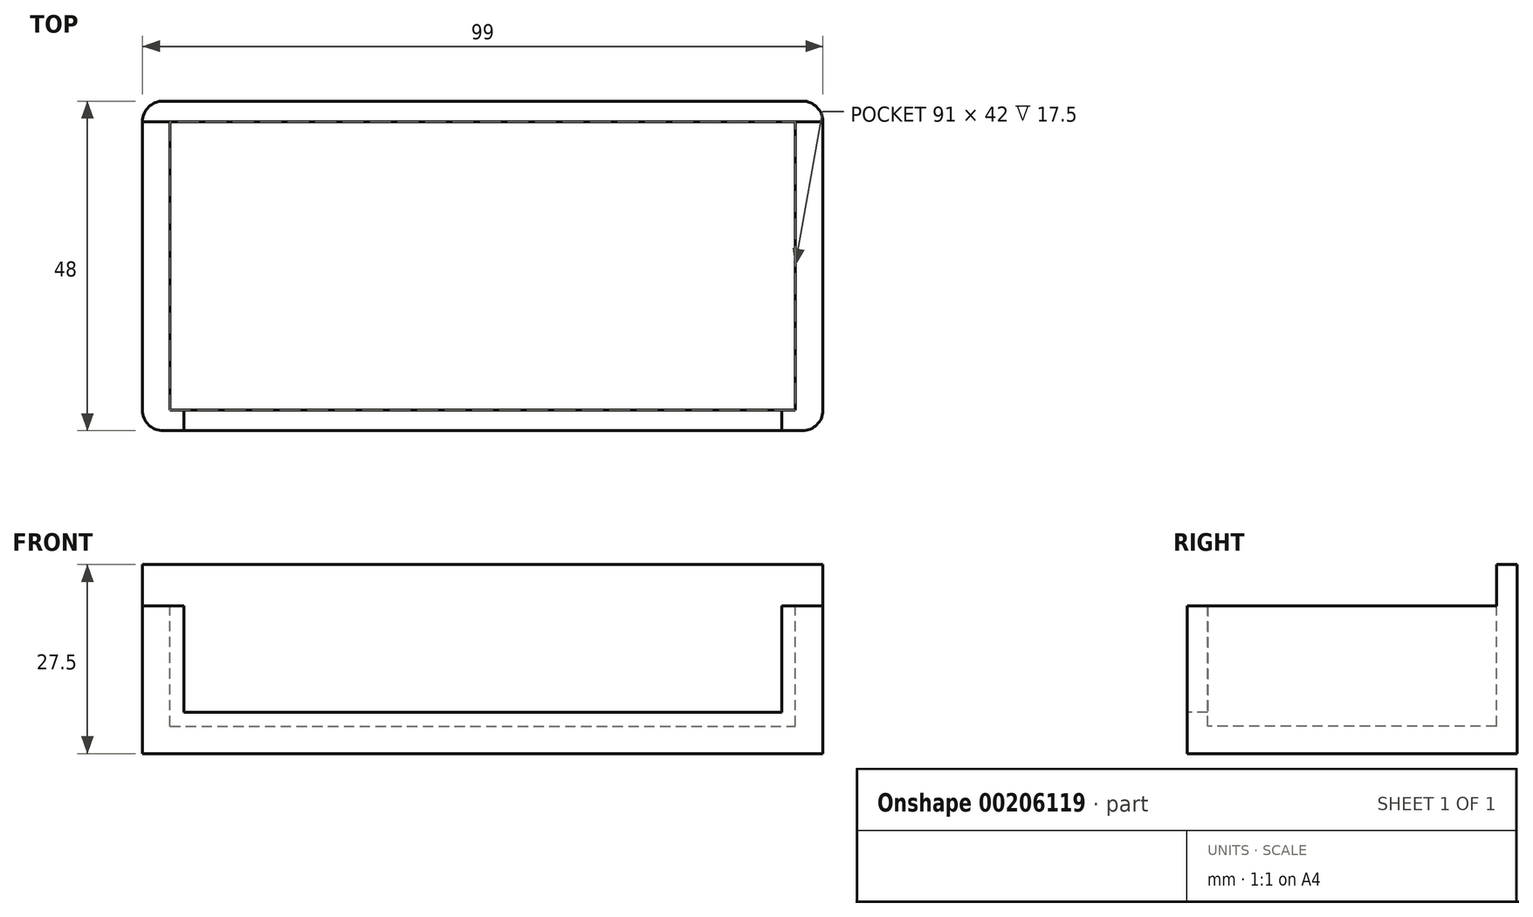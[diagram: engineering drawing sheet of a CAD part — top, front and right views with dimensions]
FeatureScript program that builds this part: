
annotation { "Feature Type Name" : "Feature", "Feature Type Description" : "" }
export const myFeature = defineFeature(function(context is Context, id is Id, definition is map)
    precondition{}
    {
        {
            var Q0;
            Q0=qCreatedBy(makeId("Front.planeOp"),FACE);
            var sketch = newSketch(context, id + "F0", { "sketchPlane" : qUnion([Q0])});
            skLineSegment(sketch, "E0.bottom", {"start": v(-49.5, 6) * mm, "end": v(49.5, 6) * mm});
            skLineSegment(sketch, "E0.top", {"start": v(-49.5, 0) * mm, "end": v(49.5, 0) * mm});
            skLineSegment(sketch, "E0.left", {"start": v(49.5, 6) * mm, "end": v(49.5, 0) * mm});
            skLineSegment(sketch, "E0.right", {"start": v(-49.5, 6) * mm, "end": v(-49.5, 0) * mm});
            skSolve(sketch);
        }
        {
            var Q0;
            Q0=makeQuery(id+"F0.imprint","IMPRINT",FACE,{"disambiguationData":[TD([[makeQuery(id+"F0.imprint","IMPRINT",EDGE,{"derivedFrom":sQuery(id+"F0.wireOp",EDGE,"E0.bottom")}),-1.0]])]});
            extrude(context, id + "F1", {"entities" : qUnion([Q0]), "depth" : 48 * mm});
        }
        {
            var Q0;
            Q0=makeQuery(id+"F1.opExtrude","SWEPT_FACE",FACE,{"disambiguationData":[OSD([sQuery(id+"F0.wireOp",EDGE,"E0.bottom")])]});
            var sketch = newSketch(context, id + "F2", { "sketchPlane" : qUnion([Q0])});
            skLineSegment(sketch, "E1.bottom", {"start": v(49.5, 0) * mm, "end": v(43.5, 0) * mm});
            skLineSegment(sketch, "E1.top", {"start": v(49.5, -48) * mm, "end": v(43.5, -48) * mm});
            skLineSegment(sketch, "E1.left", {"start": v(49.5, 0) * mm, "end": v(49.5, -48) * mm});
            skLineSegment(sketch, "E1.right", {"start": v(43.5, -3) * mm, "end": v(43.5, -48) * mm});
            skLineSegment(sketch, "E2.bottom", {"start": v(49.5, 0) * mm, "end": v(-49.5, 0) * mm});
            skLineSegment(sketch, "E2.top", {"start": v(43.5, -3) * mm, "end": v(-43.5, -3) * mm});
            skLineSegment(sketch, "E2.left", {"start": v(49.5, 0) * mm, "end": v(49.5, -3) * mm});
            skLineSegment(sketch, "E2.right", {"start": v(-49.5, 0) * mm, "end": v(-49.5, -3) * mm});
            skLineSegment(sketch, "E3.bottom", {"start": v(-49.5, 0) * mm, "end": v(-43.5, 0) * mm});
            skLineSegment(sketch, "E3.top", {"start": v(-49.5, -48) * mm, "end": v(-43.5, -48) * mm});
            skLineSegment(sketch, "E3.left", {"start": v(-49.5, 0) * mm, "end": v(-49.5, -48) * mm});
            skLineSegment(sketch, "E3.right", {"start": v(-43.5, -3) * mm, "end": v(-43.5, -48) * mm});
            skSolve(sketch);
        }
        {
            var Q0;
            Q0=makeQuery(id+"F2.imprint","IMPRINT",FACE,{"disambiguationData":[TD([[makeQuery(id+"F2.imprint","IMPRINT",EDGE,{"derivedFrom":sQuery(id+"F2.wireOp",EDGE,"E1.top")}),1.0]])]});
            extrude(context, id + "F3", {"entities" : qUnion([Q0]), "operationType" : NewBodyOperationType.ADD, "depth" : 15.5 * mm});
        }
        {
            var Q0;
            Q0=makeQuery(id+"F3.opExtrude","CAP_FACE",FACE,{"disambiguationData":[OSD([sQuery(id+"F2.wireOp",EDGE,"E1.top"),sQuery(id+"F2.wireOp",EDGE,"E1.left"),sQuery(id+"F2.wireOp",EDGE,"E1.right"),sQuery(id+"F2.wireOp",EDGE,"E2.bottom"),sQuery(id+"F2.wireOp",EDGE,"E2.top"),sQuery(id+"F2.wireOp",EDGE,"E2.left"),sQuery(id+"F2.wireOp",EDGE,"E3.bottom"),sQuery(id+"F2.wireOp",EDGE,"E3.top"),sQuery(id+"F2.wireOp",EDGE,"E3.left"),sQuery(id+"F2.wireOp",EDGE,"E3.right")])],"isStart":false});
            var sketch = newSketch(context, id + "F4", { "sketchPlane" : qUnion([Q0])});
            skLineSegment(sketch, "E4.0", {"start": v(-45.5, -3) * mm, "end": v(-45.5, -45) * mm});
            skLineSegment(sketch, "E5.0", {"start": v(45.5, -3) * mm, "end": v(45.5, -45) * mm});
            skLineSegment(sketch, "E6.0", {"start": v(-45.5, -45) * mm, "end": v(45.5, -45) * mm});
            skLineSegment(sketch, "E7.bottom", {"start": v(-49.5, 0) * mm, "end": v(49.5, 0) * mm});
            skLineSegment(sketch, "E7.top", {"start": v(-49.5, -3) * mm, "end": v(49.5, -3) * mm});
            skLineSegment(sketch, "E7.left", {"start": v(-49.5, 0) * mm, "end": v(-49.5, -3) * mm});
            skLineSegment(sketch, "E7.right", {"start": v(49.5, 0) * mm, "end": v(49.5, -3) * mm});
            skSolve(sketch);
        }
        {
            var Q0;
            {var subQ0=sQuery(id+"F4.wireOp",EDGE,"E4.0");Q0=makeQuery(id+"F4.imprint","IMPRINT",FACE,{"disambiguationData":[TD([[makeQuery(id+"F4.imprint","IMPRINT",EDGE,{"derivedFrom":subQ0}),1.0]])]});}
            var Q1;
            {var subQ0=sQuery(id+"F4.wireOp",EDGE,"E6.0");var subQ1=makeQuery(id+"F3.opExtrude","CAP_EDGE",EDGE,{"disambiguationData":[OSD([sQuery(id+"F2.wireOp",EDGE,"E3.right")])],"isStart":false});var subQ2=makeQuery(id+"F4.imprint","INTERSECT",VERTEX,{"derivedFrom":[subQ1,subQ0]});Q1=makeQuery(id+"F4.imprint","IMPRINT",FACE,{"disambiguationData":[TD([[makeQuery(id+"F4.imprint","IMPRINT",EDGE,{"disambiguationData":[TD([[subQ2,-1.0]])],"derivedFrom":subQ0}),1.0]])]});}
            var Q2;
            {var subQ0=sQuery(id+"F4.wireOp",EDGE,"E5.0");Q2=makeQuery(id+"F4.imprint","IMPRINT",FACE,{"disambiguationData":[TD([[makeQuery(id+"F4.imprint","IMPRINT",EDGE,{"derivedFrom":subQ0}),-1.0]])]});}
            extrude(context, id + "F5", {"entities" : qUnion([Q0, Q1, Q2]), "operationType" : NewBodyOperationType.REMOVE, "oppositeDirection" : true, "depth" : 17.5 * mm});
        }
        {
            var Q0;
            Q0=makeQuery(id+"F4.imprint","IMPRINT",FACE,{"disambiguationData":[TD([[makeQuery(id+"F4.imprint","IMPRINT",EDGE,{"derivedFrom":sQuery(id+"F4.wireOp",EDGE,"E7.bottom")}),-1.0]])]});
            extrude(context, id + "F6", {"entities" : qUnion([Q0]), "operationType" : NewBodyOperationType.ADD, "depth" : 6 * mm});
        }
        {
            var Q0;
            Q0=makeQuery(id+"F3.boolean.opBoolean","MERGE",EDGE,{"derivedFrom":[makeQuery(id+"F1.opExtrude","CAP_EDGE",EDGE,{"disambiguationData":[OSD([sQuery(id+"F0.wireOp",EDGE,"E0.right")])],"isStart":false}),makeQuery(id+"F3.opExtrude","SWEPT_EDGE",EDGE,{"disambiguationData":[OSD([sQuery(id+"F2.wireOp",EDGE,"E3.top"),sQuery(id+"F2.wireOp",EDGE,"E3.left")])]})]});
            var Q1;
            Q1=makeQuery(id+"F3.boolean.opBoolean","MERGE",EDGE,{"derivedFrom":[makeQuery(id+"F1.opExtrude","CAP_EDGE",EDGE,{"disambiguationData":[OSD([sQuery(id+"F0.wireOp",EDGE,"E0.left")])],"isStart":false}),makeQuery(id+"F3.opExtrude","SWEPT_EDGE",EDGE,{"disambiguationData":[OSD([sQuery(id+"F2.wireOp",EDGE,"E1.top"),sQuery(id+"F2.wireOp",EDGE,"E1.left")])]})]});
            var Q2;
            Q2=makeQuery(id+"F6.boolean.opBoolean","MERGE",EDGE,{"derivedFrom":[makeQuery(id+"F3.boolean.opBoolean","MERGE",EDGE,{"derivedFrom":[makeQuery(id+"F1.opExtrude","CAP_EDGE",EDGE,{"disambiguationData":[OSD([sQuery(id+"F0.wireOp",EDGE,"E0.left")])],"isStart":true}),makeQuery(id+"F3.opExtrude","SWEPT_EDGE",EDGE,{"disambiguationData":[OSD([sQuery(id+"F2.wireOp",EDGE,"E2.bottom"),sQuery(id+"F2.wireOp",EDGE,"E2.left")])]})]}),makeQuery(id+"F6.opExtrude","SWEPT_EDGE",EDGE,{"disambiguationData":[OSD([sQuery(id+"F4.wireOp",EDGE,"E7.bottom"),sQuery(id+"F4.wireOp",EDGE,"E7.right")])]})]});
            var Q3;
            Q3=makeQuery(id+"F6.boolean.opBoolean","MERGE",EDGE,{"derivedFrom":[makeQuery(id+"F3.boolean.opBoolean","MERGE",EDGE,{"derivedFrom":[makeQuery(id+"F1.opExtrude","CAP_EDGE",EDGE,{"disambiguationData":[OSD([sQuery(id+"F0.wireOp",EDGE,"E0.right")])],"isStart":true}),makeQuery(id+"F3.opExtrude","SWEPT_EDGE",EDGE,{"disambiguationData":[OSD([sQuery(id+"F2.wireOp",EDGE,"E3.bottom"),sQuery(id+"F2.wireOp",EDGE,"E3.left")])]})]}),makeQuery(id+"F6.opExtrude","SWEPT_EDGE",EDGE,{"disambiguationData":[OSD([sQuery(id+"F4.wireOp",EDGE,"E7.bottom"),sQuery(id+"F4.wireOp",EDGE,"E7.left")])]})]});
            fillet(context, id + "F7", {"entities" : qUnion([Q0, Q1, Q2, Q3]), "radius" : 3 * mm, "tangentPropagation" : true, "allowEdgeOverflow" : false});
        }
    });
